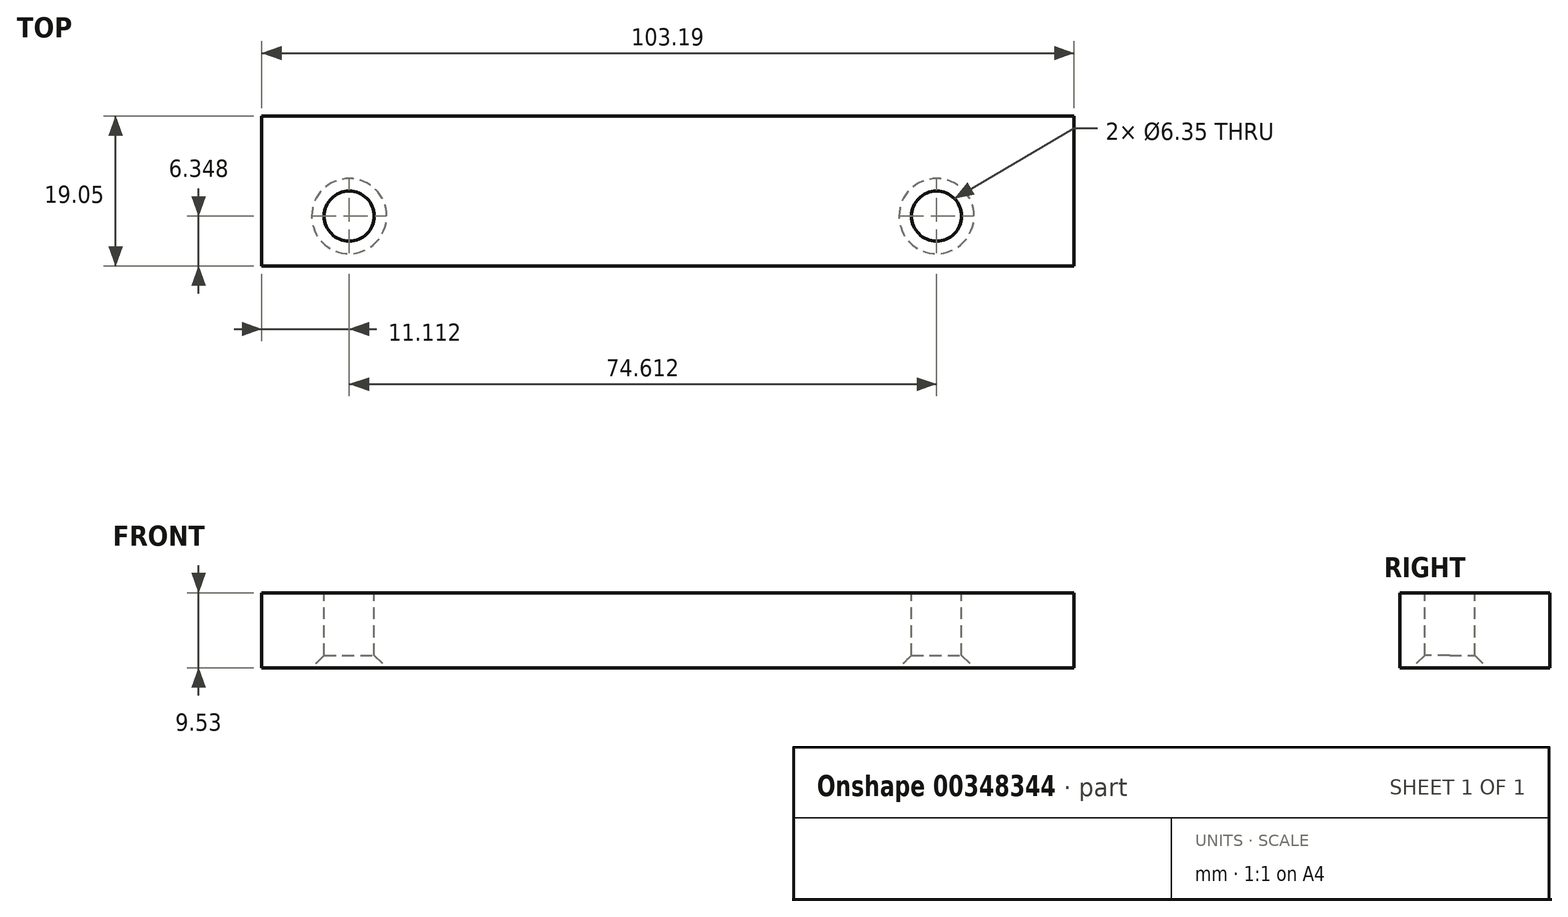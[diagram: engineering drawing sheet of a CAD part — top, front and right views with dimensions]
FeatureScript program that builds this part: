
annotation { "Feature Type Name" : "Feature", "Feature Type Description" : "" }
export const myFeature = defineFeature(function(context is Context, id is Id, definition is map)
    precondition{}
    {
        {
            var Q0;
            Q0=qCreatedBy(makeId("Top.planeOp"),FACE);
            var sketch = newSketch(context, id + "F0", { "sketchPlane" : qUnion([Q0])});
            skLineSegment(sketch, "E0.bottom", {"start": v(-56.62, -0.21) * mm, "end": v(46.57, -0.21) * mm});
            skLineSegment(sketch, "E0.top", {"start": v(-56.62, -19.26) * mm, "end": v(46.57, -19.26) * mm});
            skLineSegment(sketch, "E0.left", {"start": v(-56.62, -0.21) * mm, "end": v(-56.62, -19.26) * mm});
            skLineSegment(sketch, "E0.right", {"start": v(46.57, -0.21) * mm, "end": v(46.57, -19.26) * mm});
            skSolve(sketch);
        }
        {
            var Q0;
            Q0 = qSketchRegion(id + "F0", true);
            extrude(context, id + "F1", {"entities" : qUnion([Q0]), "depth" : 9.52 * mm});
        }
        {
            var Q0;
            Q0=makeQuery(id+"F1.opExtrude","CAP_FACE",FACE,{"disambiguationData":[OSD([sQuery(id+"F0.wireOp",EDGE,"E0.bottom"),sQuery(id+"F0.wireOp",EDGE,"E0.top"),sQuery(id+"F0.wireOp",EDGE,"E0.left"),sQuery(id+"F0.wireOp",EDGE,"E0.right")])],"isStart":false});
            var sketch = newSketch(context, id + "F2", { "sketchPlane" : qUnion([Q0])});
            skLineSegment(sketch, "E1", {"start": v(-56.62, -19.26) * mm, "end": v(-56.62, -12.91) * mm});
            skLineSegment(sketch, "E2", {"start": v(-45.5, -12.91) * mm, "end": v(-56.62, -12.91) * mm});
            skCircle(sketch, "E3", {"center": v(-45.5, -12.91) * mm, "radius": 3.18 * mm});
            skLineSegment(sketch, "E4", {"start": v(46.57, -19.26) * mm, "end": v(46.57, -12.91) * mm});
            skLineSegment(sketch, "E5", {"start": v(46.57, -12.91) * mm, "end": v(29.1, -12.91) * mm});
            skCircle(sketch, "E6", {"center": v(29.1, -12.91) * mm, "radius": 3.18 * mm});
            skSolve(sketch);
        }
        {
            var Q0;
            Q0=makeQuery(id+"F2.imprint","IMPRINT",FACE,{"disambiguationData":[TD([[makeQuery(id+"F2.imprint","IMPRINT",EDGE,{"derivedFrom":sQuery(id+"F2.wireOp",EDGE,"E3")}),1.0]])]});
            var Q1;
            Q1=makeQuery(id+"F2.imprint","IMPRINT",FACE,{"disambiguationData":[TD([[makeQuery(id+"F2.imprint","IMPRINT",EDGE,{"derivedFrom":sQuery(id+"F2.wireOp",EDGE,"E6")}),1.0]])]});
            extrude(context, id + "F3", {"entities" : qUnion([Q0, Q1]), "operationType" : NewBodyOperationType.REMOVE, "oppositeDirection" : true, "depth" : 9.52 * mm});
        }
        {
            var Q0;
            Q0=makeQuery(id+"F1.opExtrude","CAP_FACE",FACE,{"disambiguationData":[OSD([sQuery(id+"F0.wireOp",EDGE,"E0.bottom"),sQuery(id+"F0.wireOp",EDGE,"E0.top"),sQuery(id+"F0.wireOp",EDGE,"E0.left"),sQuery(id+"F0.wireOp",EDGE,"E0.right")])],"isStart":true});
            var sketch = newSketch(context, id + "F4", { "sketchPlane" : qUnion([Q0])});
            skCircle(sketch, "E7", {"center": v(-45.5, 12.91) * mm, "radius": 4.76 * mm});
            skCircle(sketch, "E8", {"center": v(29.1, 12.91) * mm, "radius": 4.76 * mm});
            skSolve(sketch);
        }
        {
            var Q0;
            Q0=sQuery(id+"F4.wireOp",VERTEX,"E7.center");
            var Q1;
            Q1=sQuery(id+"F4.wireOp",VERTEX,"E8.center");
            var Q2;
            Q2=makeQuery(id+"F1.opExtrude","SWEPT_BODY",BODY,{"disambiguationData":[OSD([sQuery(id+"F0.wireOp",EDGE,"E0.bottom"),sQuery(id+"F0.wireOp",EDGE,"E0.top"),sQuery(id+"F0.wireOp",EDGE,"E0.left"),sQuery(id+"F0.wireOp",EDGE,"E0.right")])]});
            hole(context, id + "F5", {"style" : HoleStyle.C_SINK, "endStyle" : HoleEndStyle.THROUGH, "holeDiameter" : 6.35 * mm, "cSinkDiameter" : 9.52 * mm, "cSinkAngle" : 90 * degree, "isTappedThrough" : true, "tappedDepth" : 12.7 * mm, "tapClearance" : 3, "locations" : qUnion([Q0, Q1]), "scope" : qUnion([Q2])});
        }
    });
